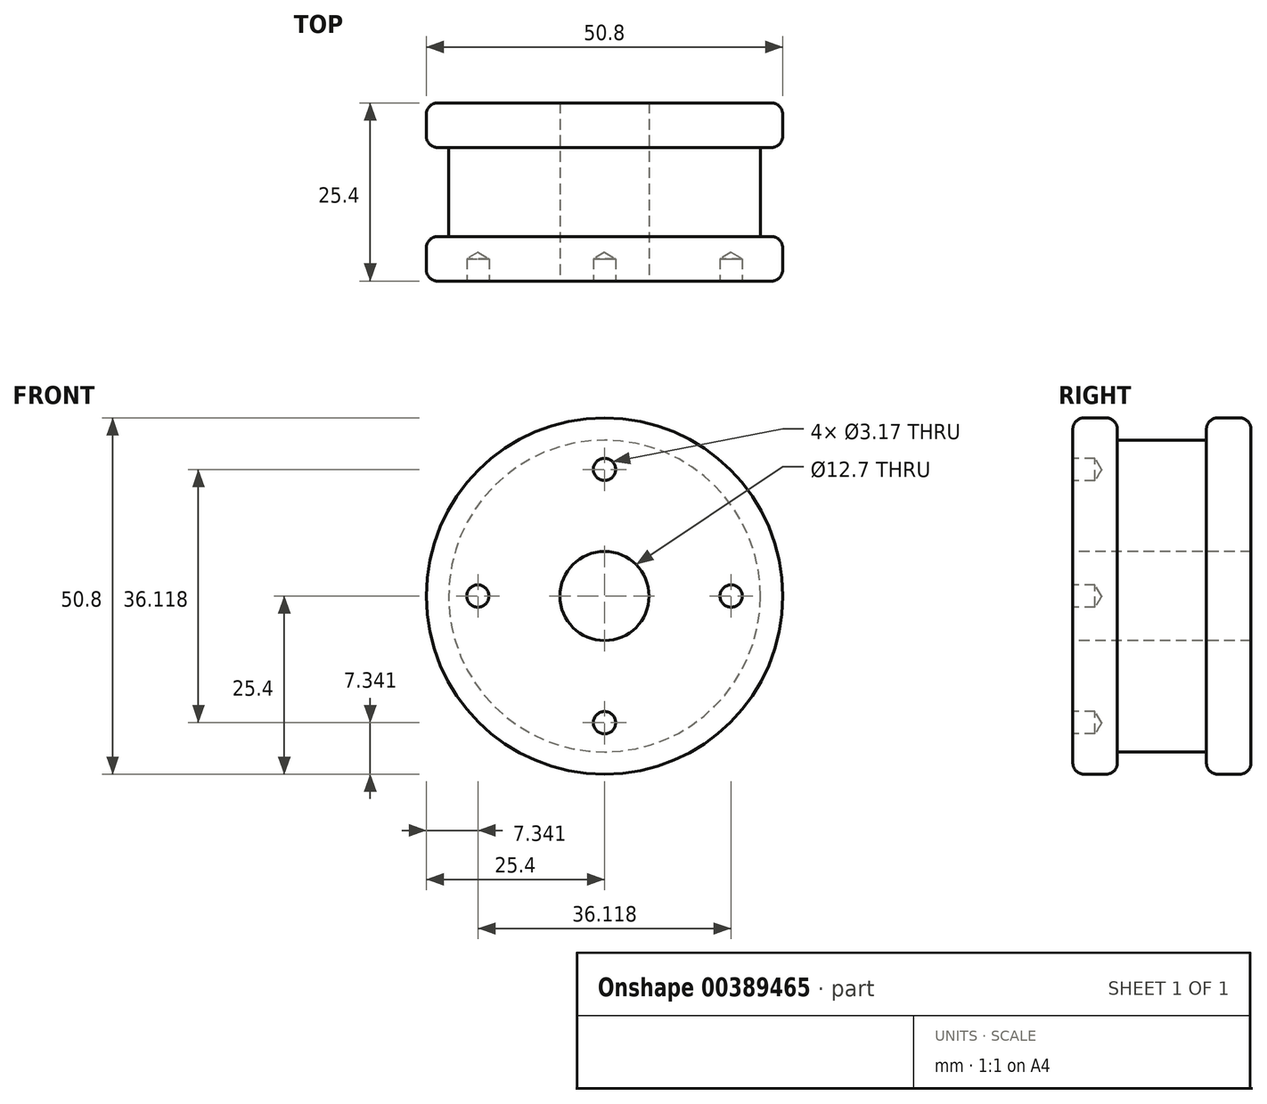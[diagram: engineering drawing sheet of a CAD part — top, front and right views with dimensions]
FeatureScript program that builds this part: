
annotation { "Feature Type Name" : "Feature", "Feature Type Description" : "" }
export const myFeature = defineFeature(function(context is Context, id is Id, definition is map)
    precondition{}
    {
        {
            var Q0;
            Q0=qCreatedBy(makeId("Front.planeOp"),FACE);
            var sketch = newSketch(context, id + "F0", { "sketchPlane" : qUnion([Q0])});
            skCircle(sketch, "E0", {"center": v(0, 0) * mm, "radius": 25.4 * mm});
            skSolve(sketch);
        }
        {
            var Q0;
            Q0 = qSketchRegion(id + "F0", true);
            extrude(context, id + "F1", {"entities" : qUnion([Q0]), "depth" : 6.35 * mm});
        }
        {
            var Q0;
            Q0=makeQuery(id+"F1.opExtrude","CAP_FACE",FACE,{"disambiguationData":[OSD([sQuery(id+"F0.wireOp",EDGE,"E0")])],"isStart":true});
            var sketch = newSketch(context, id + "F2", { "sketchPlane" : qUnion([Q0])});
            skCircle(sketch, "E1", {"center": v(0, 0) * mm, "radius": 22.23 * mm});
            skSolve(sketch);
        }
        {
            var Q0;
            Q0 = qSketchRegion(id + "F2", true);
            extrude(context, id + "F3", {"entities" : qUnion([Q0]), "operationType" : NewBodyOperationType.ADD, "depth" : 12.7 * mm});
        }
        {
            var Q0;
            Q0=makeQuery(id+"F3.opExtrude","CAP_FACE",FACE,{"disambiguationData":[OSD([sQuery(id+"F2.wireOp",EDGE,"E1")])],"isStart":false});
            var sketch = newSketch(context, id + "F4", { "sketchPlane" : qUnion([Q0])});
            skCircle(sketch, "E2", {"center": v(0, 0) * mm, "radius": 25.4 * mm});
            skSolve(sketch);
        }
        {
            var Q0;
            Q0 = qSketchRegion(id + "F4", true);
            extrude(context, id + "F5", {"entities" : qUnion([Q0]), "operationType" : NewBodyOperationType.ADD, "depth" : 6.35 * mm});
        }
        {
            var Q0;
            Q0=makeQuery(id+"F1.opExtrude","CAP_EDGE",EDGE,{"disambiguationData":[OSD([sQuery(id+"F0.wireOp",EDGE,"E0")])],"isStart":false});
            var Q1;
            Q1=makeQuery(id+"F5.opExtrude","CAP_EDGE",EDGE,{"disambiguationData":[OSD([sQuery(id+"F4.wireOp",EDGE,"E2")])],"isStart":false});
            var Q2;
            Q2=makeQuery(id+"F1.opExtrude","CAP_EDGE",EDGE,{"disambiguationData":[OSD([sQuery(id+"F0.wireOp",EDGE,"E0")])],"isStart":true});
            var Q3;
            Q3=makeQuery(id+"F5.opExtrude","CAP_EDGE",EDGE,{"disambiguationData":[OSD([sQuery(id+"F4.wireOp",EDGE,"E2")])],"isStart":true});
            fillet(context, id + "F6", {"entities" : qUnion([Q0, Q1, Q2, Q3]), "radius" : 1.6 * mm, "tangentPropagation" : true, "allowEdgeOverflow" : false});
        }
        {
            var Q0;
            Q0=makeQuery(id+"F1.opExtrude","CAP_FACE",FACE,{"disambiguationData":[OSD([sQuery(id+"F0.wireOp",EDGE,"E0")])],"isStart":false});
            var sketch = newSketch(context, id + "F7", { "sketchPlane" : qUnion([Q0])});
            skPoint(sketch, "E3", {"position": v(0, 18.06) * mm});
            skPoint(sketch, "E4.1.0", {"position": v(-18.06, 0) * mm});
            skPoint(sketch, "E4.2.0", {"position": v(0, -18.06) * mm});
            skPoint(sketch, "E4.3.0", {"position": v(18.06, 0) * mm});
            skPoint(sketch, "E4.center", {"position": v(0, 0) * mm});
            skSolve(sketch);
        }
        {
            var Q0;
            Q0=sQuery(id+"F7.wireOp",VERTEX,"E3");
            var Q1;
            Q1=sQuery(id+"F7.wireOp",VERTEX,"E4.1.0");
            var Q2;
            Q2=sQuery(id+"F7.wireOp",VERTEX,"E4.2.0");
            var Q3;
            Q3=sQuery(id+"F7.wireOp",VERTEX,"E4.3.0");
            var Q4;
            Q4=makeQuery(id+"F1.opExtrude","SWEPT_BODY",BODY,{"disambiguationData":[OSD([sQuery(id+"F0.wireOp",EDGE,"E0")])]});
            hole(context, id + "F8", {"style" : HoleStyle.SIMPLE, "endStyle" : HoleEndStyle.BLIND, "holeDiameter" : 3.17 * mm, "holeDepth" : 3.17 * mm, "isTappedThrough" : true, "tappedDepth" : 12.7 * mm, "tapClearance" : 3, "locations" : qUnion([Q0, Q1, Q2, Q3]), "scope" : qUnion([Q4])});
        }
        {
            var Q0;
            Q0=makeQuery(id+"F1.opExtrude","CAP_FACE",FACE,{"disambiguationData":[OSD([sQuery(id+"F0.wireOp",EDGE,"E0")])],"isStart":false});
            var sketch = newSketch(context, id + "F9", { "sketchPlane" : qUnion([Q0])});
            skCircle(sketch, "E5", {"center": v(0, 0) * mm, "radius": 6.35 * mm});
            skSolve(sketch);
        }
        {
            var Q0;
            Q0=sQuery(id+"F9.wireOp",VERTEX,"E5.center");
            var Q1;
            Q1=makeQuery(id+"F1.opExtrude","SWEPT_BODY",BODY,{"disambiguationData":[OSD([sQuery(id+"F0.wireOp",EDGE,"E0")])]});
            hole(context, id + "F10", {"style" : HoleStyle.SIMPLE, "endStyle" : HoleEndStyle.THROUGH, "holeDiameter" : 12.7 * mm, "isTappedThrough" : true, "tappedDepth" : 12.7 * mm, "tapClearance" : 3, "locations" : qUnion([Q0]), "scope" : qUnion([Q1])});
        }
    });
